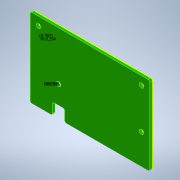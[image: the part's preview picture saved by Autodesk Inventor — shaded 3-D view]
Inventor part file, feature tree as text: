
AUTODESK INVENTOR PART (.ipt)
format: ipt  version: 2021 (Build 250183000, 183)  size: 184,832 bytes
history: native  units: mm
features: extrude x3, sketch x3, fillet x1, other x1
ambient origin geometry x8: Origin, YZ Plane, XZ Plane, XY Plane, X Axis, Y Axis, Z Axis, Center Point
bodies: Solid1 (feature_tree)
feature tree (8):
  extrude  "Extrusion1"  Depth=71.4mm
  extrude  "Extrusion2"  Depth=50.8mm
  extrude  "Extrusion3"  Depth=7.0mm
  fillet  "Fillet1"  Radius=1.6mm
  other  "PWR_PCBA_OUTLINE"
  sketch  "Sketch1"  dims[d0=47.0mm d1=71.4mm]
  sketch  "Sketch2"  dims[d2=1.6mm d3=0.0mm d4=50.8mm]
  sketch  "Sketch3"  dims[d5=7.2mm d6=7.0mm d7=1.6mm d8=0.0mm d9=2.75mm d10=2.75mm d11=2.75mm d12=5.0mm d13=5.0mm d14=5.0mm d15=5.0mm d16=5.0mm d17=18.0mm d18=0.0mm d19=0.0mm d20=2.75mm d21=0.0mm d22=7.2mm d23=3.6mm d28=1.0mm d29=0.7874mm d30=0.3937mm d31=0.3937mm d32=0.7874mm]
